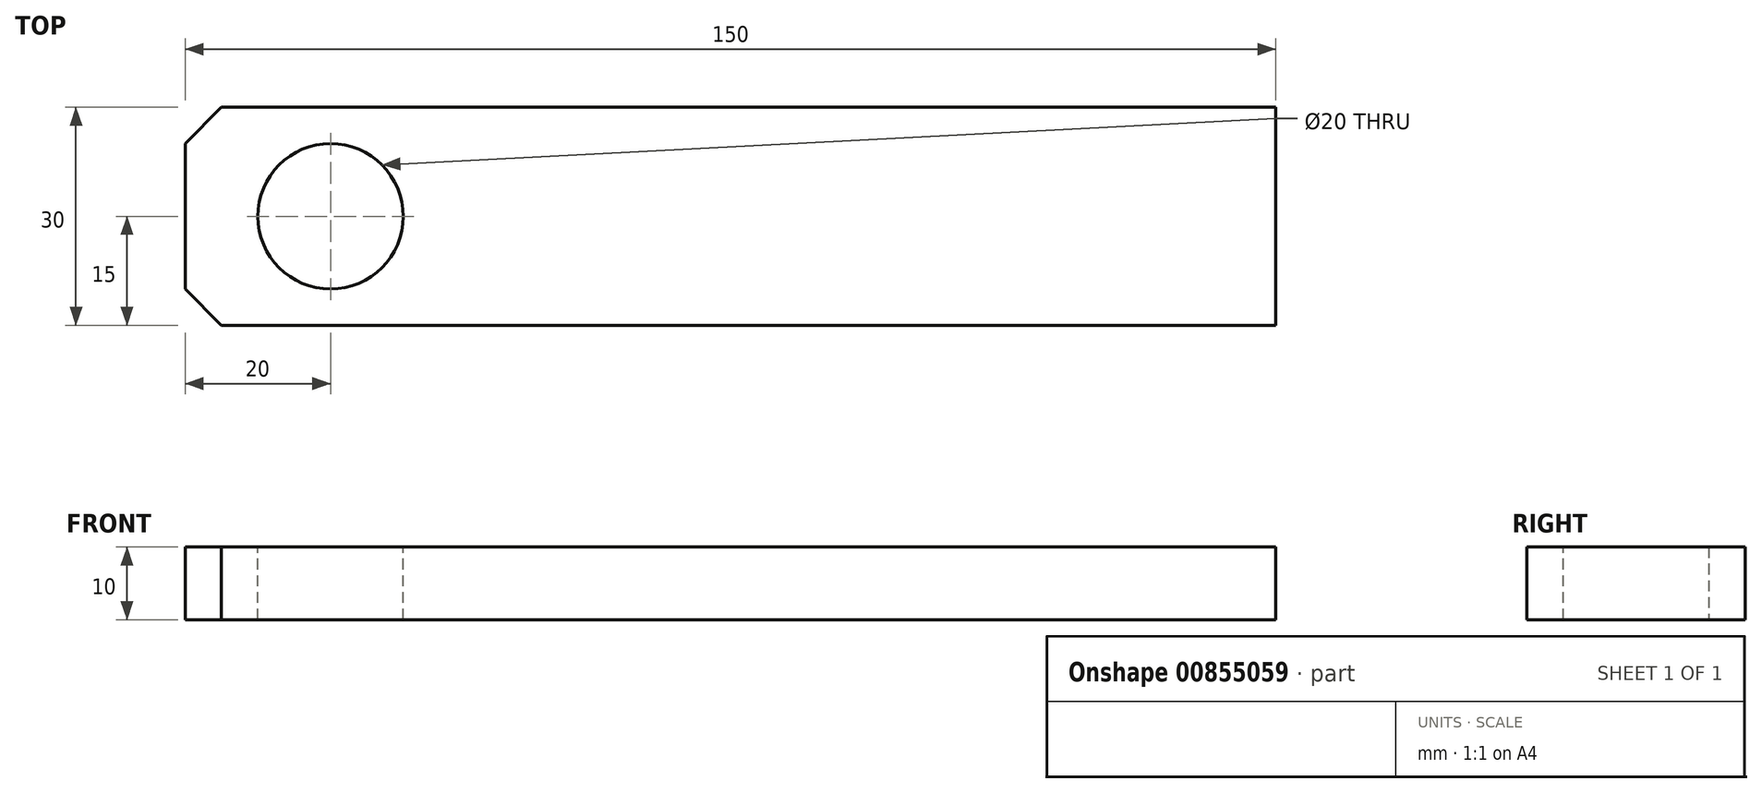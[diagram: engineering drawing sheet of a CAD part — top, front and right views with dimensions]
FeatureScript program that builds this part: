
annotation { "Feature Type Name" : "Feature", "Feature Type Description" : "" }
export const myFeature = defineFeature(function(context is Context, id is Id, definition is map)
    precondition{}
    {
        {
            var Q0;
            Q0=qCreatedBy(makeId("Top.planeOp"),FACE);
            var sketch = newSketch(context, id + "F0", { "sketchPlane" : qUnion([Q0])});
            skLineSegment(sketch, "E0.bottom", {"start": v(75, -15) * mm, "end": v(-75, -15) * mm});
            skLineSegment(sketch, "E0.top", {"start": v(75, 15) * mm, "end": v(-75, 15) * mm});
            skLineSegment(sketch, "E0.left", {"start": v(75, -15) * mm, "end": v(75, 15) * mm});
            skLineSegment(sketch, "E0.right", {"start": v(-75, -15) * mm, "end": v(-75, 15) * mm});
            skPoint(sketch, "E0.middle", {"position": v(0, 0) * mm});
            skSolve(sketch);
        }
        {
            var Q0;
            Q0=makeQuery(id+"F0.imprint","IMPRINT",FACE,{"disambiguationData":[TD([[makeQuery(id+"F0.imprint","IMPRINT",EDGE,{"derivedFrom":sQuery(id+"F0.wireOp",EDGE,"E0.bottom")}),-1.0]])]});
            extrude(context, id + "F1", {"entities" : qUnion([Q0]), "depth" : 10 * mm, "offsetDistance" : 25 * mm});
        }
        {
            var Q0;
            Q0=makeQuery(id+"F1.opExtrude","CAP_FACE",FACE,{"disambiguationData":[OSD([sQuery(id+"F0.wireOp",EDGE,"E0.bottom"),sQuery(id+"F0.wireOp",EDGE,"E0.top"),sQuery(id+"F0.wireOp",EDGE,"E0.left"),sQuery(id+"F0.wireOp",EDGE,"E0.right")])],"isStart":false});
            var sketch = newSketch(context, id + "F2", { "sketchPlane" : qUnion([Q0])});
            skPoint(sketch, "E1", {"position": v(-55, 0) * mm});
            skSolve(sketch);
        }
        {
            var Q0;
            Q0=sQuery(id+"F2.wireOp",VERTEX,"E1");
            var Q1;
            Q1=makeQuery(id+"F1.opExtrude","SWEPT_BODY",BODY,{"disambiguationData":[OSD([sQuery(id+"F0.wireOp",EDGE,"E0.bottom"),sQuery(id+"F0.wireOp",EDGE,"E0.top"),sQuery(id+"F0.wireOp",EDGE,"E0.left"),sQuery(id+"F0.wireOp",EDGE,"E0.right")])]});
            hole(context, id + "F3", {"style" : HoleStyle.SIMPLE, "endStyle" : HoleEndStyle.THROUGH, "holeDiameter" : 20 * mm, "majorDiameter" : 5 * mm, "isTappedThrough" : true, "tappedDepth" : 12 * mm, "tapClearance" : 3, "locations" : qUnion([Q0]), "scope" : qUnion([Q1])});
        }
        {
            var Q0;
            Q0=makeQuery(id+"F1.opExtrude","SWEPT_EDGE",EDGE,{"disambiguationData":[OSD([sQuery(id+"F0.wireOp",EDGE,"E0.bottom"),sQuery(id+"F0.wireOp",EDGE,"E0.right")])]});
            var Q1;
            Q1=makeQuery(id+"F1.opExtrude","SWEPT_EDGE",EDGE,{"disambiguationData":[OSD([sQuery(id+"F0.wireOp",EDGE,"E0.top"),sQuery(id+"F0.wireOp",EDGE,"E0.right")])]});
            chamfer(context, id + "F4", {"entities" : qUnion([Q0, Q1]), "width" : 5 * mm, "tangentPropagation" : true});
        }
    });
